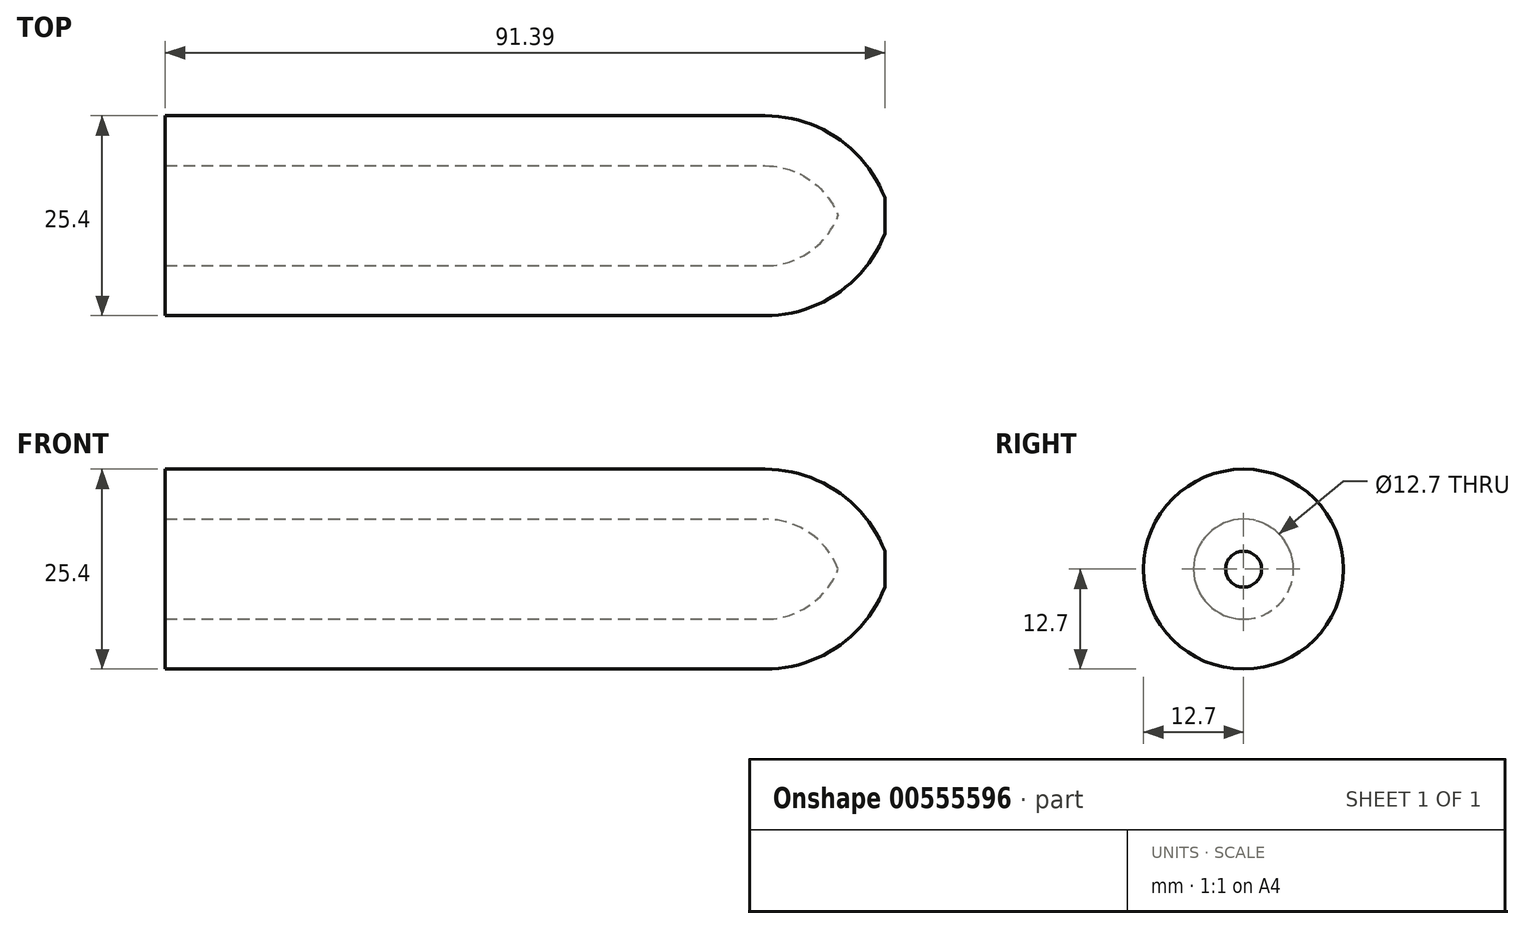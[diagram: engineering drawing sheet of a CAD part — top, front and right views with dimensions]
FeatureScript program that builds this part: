
annotation { "Feature Type Name" : "Feature", "Feature Type Description" : "" }
export const myFeature = defineFeature(function(context is Context, id is Id, definition is map)
    precondition{}
    {
        {
            var Q0;
            Q0=qCreatedBy(makeId("Front.planeOp"),FACE);
            var sketch = newSketch(context, id + "F0", { "sketchPlane" : qUnion([Q0])});
            skLineSegment(sketch, "E0", {"start": v(0, 0) * mm, "end": v(-76.2, 0) * mm});
            skArc(sketch, "E1", {"start": v(0, 0) * mm, "mid": v(5.62, 1.74) * mm, "end": v(9.26, 6.35) * mm});
            skLineSegment(sketch, "E2.0", {"start": v(0, -6.35) * mm, "end": v(-76.2, -6.35) * mm});
            skArc(sketch, "E2.1", {"start": v(0, -6.35) * mm, "mid": v(9.2, -3.5) * mm, "end": v(15.19, 4.06) * mm});
            skLineSegment(sketch, "E3", {"start": v(15.19, 4.06) * mm, "end": v(15.19, 6.35) * mm});
            skLineSegment(sketch, "E4", {"start": v(15.19, 6.35) * mm, "end": v(9.26, 6.35) * mm});
            skLineSegment(sketch, "E5", {"start": v(-76.2, 0) * mm, "end": v(-76.2, -6.35) * mm});
            skSolve(sketch);
        }
        {
            var Q0;
            Q0=makeQuery(id+"F0.imprint","IMPRINT",FACE,{"disambiguationData":[TD([[makeQuery(id+"F0.imprint","IMPRINT",EDGE,{"derivedFrom":sQuery(id+"F0.wireOp",EDGE,"E0")}),1.0]])]});
            var Q1;
            Q1=sQuery(id+"F0.wireOp",EDGE,"E4");
            revolve(context, id + "F1", {"entities" : qUnion([Q0]), "axis" : qUnion([Q1]), "revolveType" : RevolveType.FULL});
        }
    });
